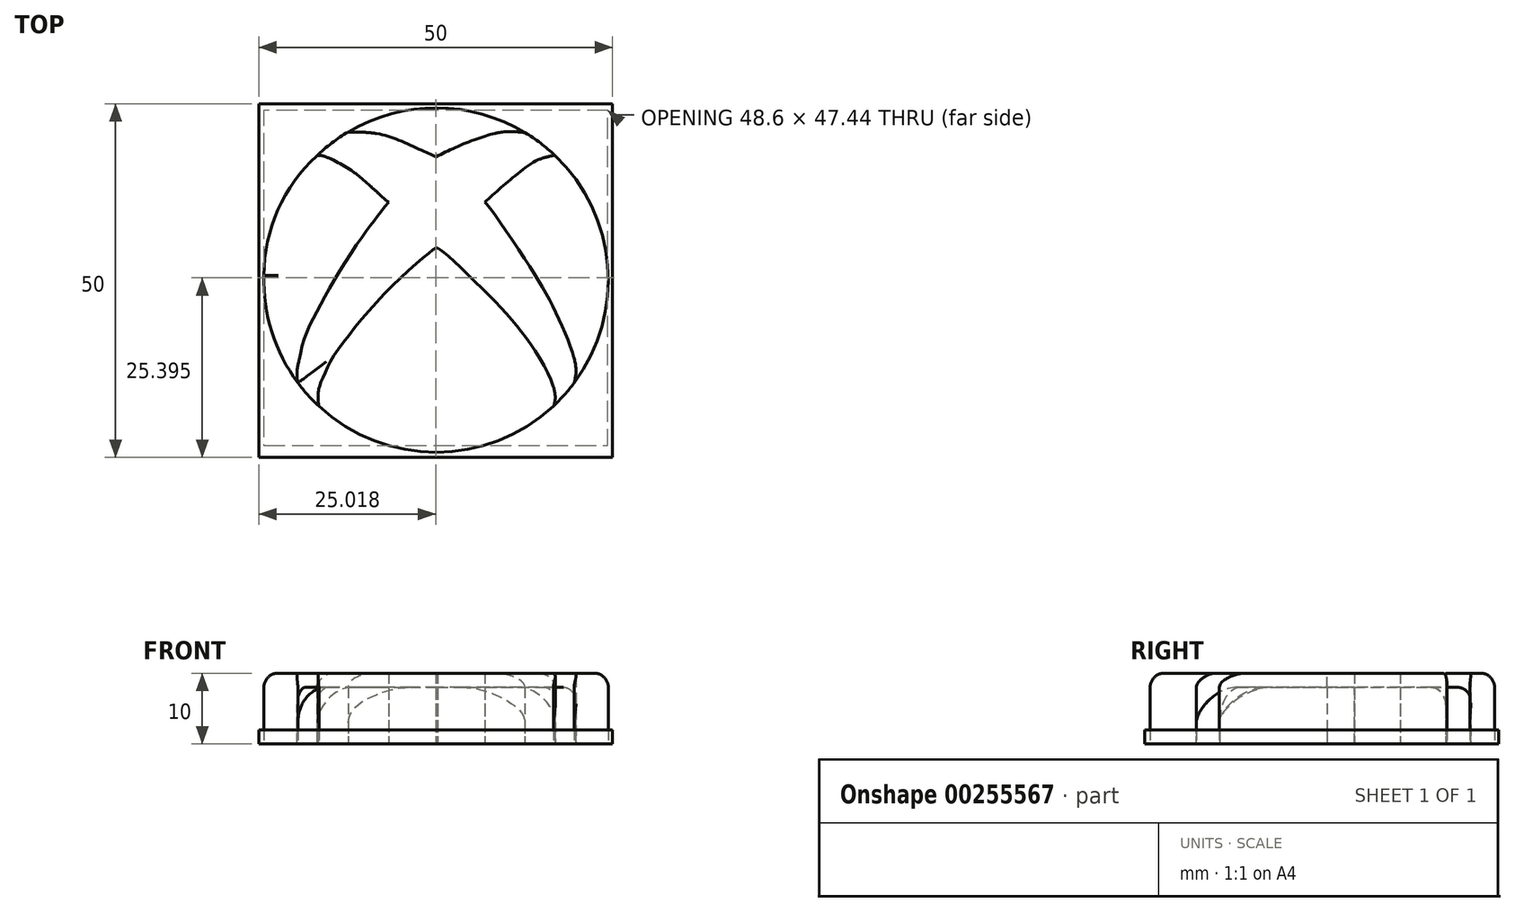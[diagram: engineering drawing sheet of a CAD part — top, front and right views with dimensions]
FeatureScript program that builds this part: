
annotation { "Feature Type Name" : "Feature", "Feature Type Description" : "" }
export const myFeature = defineFeature(function(context is Context, id is Id, definition is map)
    precondition{}
    {
        {
            var Q0;
            Q0=qCreatedBy(makeId("Top.planeOp"),FACE);
            var sketch = newSketch(context, id + "F0", { "sketchPlane" : qUnion([Q0])});
            skArc(sketch, "E0", {"start": v(0.72, 25.77) * mm, "mid": v(47.31, 15.23) * mm, "end": v(8.19, 42.64) * mm});
            skArc(sketch, "E1", {"start": v(8.19, 42.64) * mm, "mid": v(2.7, 34.98) * mm, "end": v(0.72, 25.77) * mm});
            skFitSpline(sketch, "E2", {"points": [v(8.19, 42.64) * mm, v(9.05, 42.64) * mm, v(11.26, 41.67) * mm, v(14.14, 39.78) * mm, v(18.23, 36.16) * mm, v(18.33, 36.1) * mm], "startDerivative": vector(5.76, 0.85) * mm, "endDerivative": vector(1.28, -0.26) * mm});
            skFitSpline(sketch, "E3", {"points": [v(18.33, 36.1) * mm, v(16.77, 34.08) * mm, v(15.03, 31.77) * mm, v(11.17, 25.93) * mm, v(8.19, 20.55) * mm, v(6.44, 16.85) * mm, v(5.64, 13.57) * mm, v(5.38, 11.98) * mm, v(5.52, 10.56) * mm, v(5.53, 10.55) * mm], "startDerivative": vector(-14.68, -19.2) * mm, "endDerivative": vector(1.1, -0.72) * mm});
            skFitSpline(sketch, "E4", {"points": [v(8.5, 7.24) * mm, v(8.37, 8.34) * mm, v(8.52, 9.84) * mm, v(9.16, 11.53) * mm, v(10.26, 13.8) * mm, v(13.18, 17.86) * mm, v(18.97, 24.37) * mm, v(23.99, 28.86) * mm, v(25.07, 29.65) * mm, v(25.26, 29.6) * mm], "startDerivative": vector(-2.52, 14.49) * mm, "endDerivative": vector(5.4, -3.15) * mm});
            skFitSpline(sketch, "E5", {"points": [v(25.26, 29.6) * mm, v(26.45, 28.76) * mm, v(31.47, 24) * mm, v(35.75, 19.48) * mm, v(38.85, 15.4) * mm, v(41.46, 10.55) * mm, v(41.89, 8.19) * mm, v(41.66, 7.28) * mm], "startDerivative": vector(11.02, -6.85) * mm, "endDerivative": vector(-4.1, -11.3) * mm});
            skFitSpline(sketch, "E6", {"points": [v(44.58, 10.55) * mm, v(44.83, 12.13) * mm, v(44.3, 14.98) * mm, v(41.66, 21.15) * mm, v(37.47, 28.27) * mm, v(31.95, 36.1) * mm, v(31.9, 36.1) * mm], "startDerivative": vector(3.3, 14.03) * mm, "endDerivative": vector(-2.08, -1.26) * mm});
            skFitSpline(sketch, "E7", {"points": [v(31.95, 36.1) * mm, v(33.85, 37.83) * mm, v(36.4, 39.96) * mm, v(39.25, 41.98) * mm, v(41.83, 42.72) * mm], "startDerivative": vector(7.9, 7.3) * mm, "endDerivative": vector(10.93, 2.03) * mm});
            skLineSegment(sketch, "E8.bottom", {"start": v(0, 50) * mm, "end": v(50, 50) * mm});
            skLineSegment(sketch, "E8.top", {"start": v(0, 0) * mm, "end": v(50, 0) * mm});
            skLineSegment(sketch, "E8.left", {"start": v(0, 50) * mm, "end": v(0, 0) * mm});
            skLineSegment(sketch, "E8.right", {"start": v(50, 50) * mm, "end": v(50, 0) * mm});
            skFitSpline(sketch, "E9", {"points": [v(37.62, 45.94) * mm, v(35.23, 46.07) * mm, v(32.55, 45.61) * mm, v(28.56, 44.16) * mm, v(25.04, 42.5) * mm], "startDerivative": vector(-11.13, 1.18) * mm, "endDerivative": vector(-12.47, -6.15) * mm});
            skFitSpline(sketch, "E10", {"points": [v(25.04, 42.5) * mm, v(23.24, 43.32) * mm, v(19.67, 44.9) * mm, v(16.5, 45.82) * mm, v(12.64, 46.02) * mm], "startDerivative": vector(-8.28, 3.68) * mm, "endDerivative": vector(-14.56, 0.03) * mm});
            skSolve(sketch);
        }
        {
            var Q0;
            {var subQ0=sQuery(id+"F0.wireOp",EDGE,"E1");Q0=makeQuery(id+"F0.imprint","IMPRINT",FACE,{"disambiguationData":[TD([[makeQuery(id+"F0.imprint","IMPRINT",EDGE,{"derivedFrom":subQ0}),1.0]])]});}
            var Q1;
            {var subQ0=sQuery(id+"F0.wireOp",EDGE,"E9");Q1=makeQuery(id+"F0.imprint","IMPRINT",FACE,{"disambiguationData":[TD([[makeQuery(id+"F0.imprint","IMPRINT",EDGE,{"derivedFrom":subQ0}),-1.0]])]});}
            var Q2;
            {var subQ3=sQuery(id+"F0.wireOp",EDGE,"E7");Q2=makeQuery(id+"F0.imprint","IMPRINT",FACE,{"disambiguationData":[TD([[makeQuery(id+"F0.imprint","IMPRINT",EDGE,{"derivedFrom":subQ3}),-1.0]])]});}
            var Q3;
            {var subQ0=sQuery(id+"F0.wireOp",EDGE,"E4");Q3=makeQuery(id+"F0.imprint","IMPRINT",FACE,{"disambiguationData":[TD([[makeQuery(id+"F0.imprint","IMPRINT",EDGE,{"derivedFrom":subQ0}),-1.0]])]});}
            extrude(context, id + "F1", {"entities" : qUnion([Q0, Q1, Q2, Q3]), "depth" : 10 * mm});
        }
        {
            var Q0;
            {var subQ4=sQuery(id+"F0.wireOp",EDGE,"E2");Q0=makeQuery(id+"F0.imprint","IMPRINT",FACE,{"disambiguationData":[TD([[makeQuery(id+"F0.imprint","IMPRINT",EDGE,{"derivedFrom":subQ4}),1.0]])]});}
            extrude(context, id + "F2", {"entities" : qUnion([Q0]), "depth" : 8 * mm});
        }
        {
            var Q0;
            Q0=makeQuery(id+"F1.opExtrude","CAP_EDGE",EDGE,{"disambiguationData":[OSD([sQuery(id+"F0.wireOp",EDGE,"E1")])],"isStart":false});
            var Q1;
            {var subQ0=sQuery(id+"F0.wireOp",EDGE,"E0");Q1=makeQuery(id+"F1.opExtrude","CAP_EDGE",EDGE,{"disambiguationData":[OSD([subQ0]),TDD([makeQuery(id+"F0.imprint","IMPRINT",EDGE,{"disambiguationData":[TD([[makeQuery(id+"F0.imprint","INTERSECT",VERTEX,{"derivedFrom":[subQ0,sQuery(id+"F0.wireOp",EDGE,"E4")]}),-1.0]])],"derivedFrom":subQ0})])],"isStart":false});}
            var Q2;
            {var subQ0=sQuery(id+"F0.wireOp",EDGE,"E0");Q2=makeQuery(id+"F1.opExtrude","CAP_EDGE",EDGE,{"disambiguationData":[OSD([subQ0]),TDD([makeQuery(id+"F0.imprint","IMPRINT",EDGE,{"disambiguationData":[TD([[makeQuery(id+"F0.imprint","INTERSECT",VERTEX,{"derivedFrom":[subQ0,sQuery(id+"F0.wireOp",EDGE,"E6")]}),-1.0]])],"derivedFrom":subQ0})])],"isStart":false});}
            var Q3;
            {var subQ0=sQuery(id+"F0.wireOp",EDGE,"E0");Q3=makeQuery(id+"F1.opExtrude","CAP_EDGE",EDGE,{"disambiguationData":[OSD([subQ0]),TDD([makeQuery(id+"F0.imprint","IMPRINT",EDGE,{"disambiguationData":[TD([[makeQuery(id+"F0.imprint","INTERSECT",VERTEX,{"derivedFrom":[subQ0,sQuery(id+"F0.wireOp",EDGE,"E9")]}),-1.0]])],"derivedFrom":subQ0})])],"isStart":false});}
            fillet(context, id + "F3", {"entities" : qUnion([Q0, Q1, Q2, Q3]), "radius" : 2 * mm, "tangentPropagation" : true, "allowEdgeOverflow" : false});
        }
        {
            var Q0;
            {var subQ0=sQuery(id+"F0.wireOp",EDGE,"E3");var subQ1=sQuery(id+"F0.wireOp",EDGE,"E0");var subQ2=makeQuery(id+"F0.imprint","INTERSECT",VERTEX,{"disambiguationData":[OD(0.0)],"derivedFrom":[subQ1,subQ0]});Q0=makeQuery(id+"F2.opExtrude","CAP_EDGE",EDGE,{"disambiguationData":[OSD([subQ1]),TDD([makeQuery(id+"F0.imprint","IMPRINT",EDGE,{"disambiguationData":[TD([[subQ2,1.0]])],"derivedFrom":subQ1}),makeQuery(id+"F0.imprint","IMPRINT",EDGE,{"disambiguationData":[TD([[subQ2,-1.0]])],"derivedFrom":subQ1})])],"isStart":false});}
            var Q1;
            {var subQ0=sQuery(id+"F0.wireOp",EDGE,"E0");Q1=makeQuery(id+"F2.opExtrude","CAP_EDGE",EDGE,{"disambiguationData":[OSD([subQ0]),TDD([makeQuery(id+"F0.imprint","IMPRINT",EDGE,{"disambiguationData":[TD([[makeQuery(id+"F0.imprint","INTERSECT",VERTEX,{"derivedFrom":[subQ0,sQuery(id+"F0.wireOp",EDGE,"E5")]}),-1.0]])],"derivedFrom":subQ0})])],"isStart":false});}
            var Q2;
            {var subQ0=sQuery(id+"F0.wireOp",EDGE,"E0");Q2=makeQuery(id+"F2.opExtrude","CAP_EDGE",EDGE,{"disambiguationData":[OSD([subQ0]),TDD([makeQuery(id+"F0.imprint","IMPRINT",EDGE,{"disambiguationData":[TD([[makeQuery(id+"F0.imprint","INTERSECT",VERTEX,{"derivedFrom":[subQ0,sQuery(id+"F0.wireOp",EDGE,"E7")]}),-1.0]])],"derivedFrom":subQ0})])],"isStart":false});}
            var Q3;
            {var subQ0=sQuery(id+"F0.wireOp",EDGE,"E0");Q3=makeQuery(id+"F2.opExtrude","CAP_EDGE",EDGE,{"disambiguationData":[OSD([subQ0]),TDD([makeQuery(id+"F0.imprint","IMPRINT",EDGE,{"disambiguationData":[TD([[makeQuery(id+"F0.imprint","INTERSECT",VERTEX,{"derivedFrom":[subQ0,sQuery(id+"F0.wireOp",EDGE,"E10")]}),-1.0]])],"derivedFrom":subQ0})])],"isStart":false});}
            fillet(context, id + "F4", {"entities" : qUnion([Q0, Q1, Q2, Q3]), "radius" : 5 * mm, "tangentPropagation" : true, "allowEdgeOverflow" : false});
        }
        {
            var Q0;
            {var subQ0=sQuery(id+"F0.wireOp",EDGE,"E1");Q0=makeQuery(id+"F0.imprint","IMPRINT",FACE,{"disambiguationData":[TD([[makeQuery(id+"F0.imprint","IMPRINT",EDGE,{"derivedFrom":subQ0}),-1.0]])]});}
            extrude(context, id + "F5", {"entities" : qUnion([Q0]), "depth" : 2 * mm});
        }
    });
